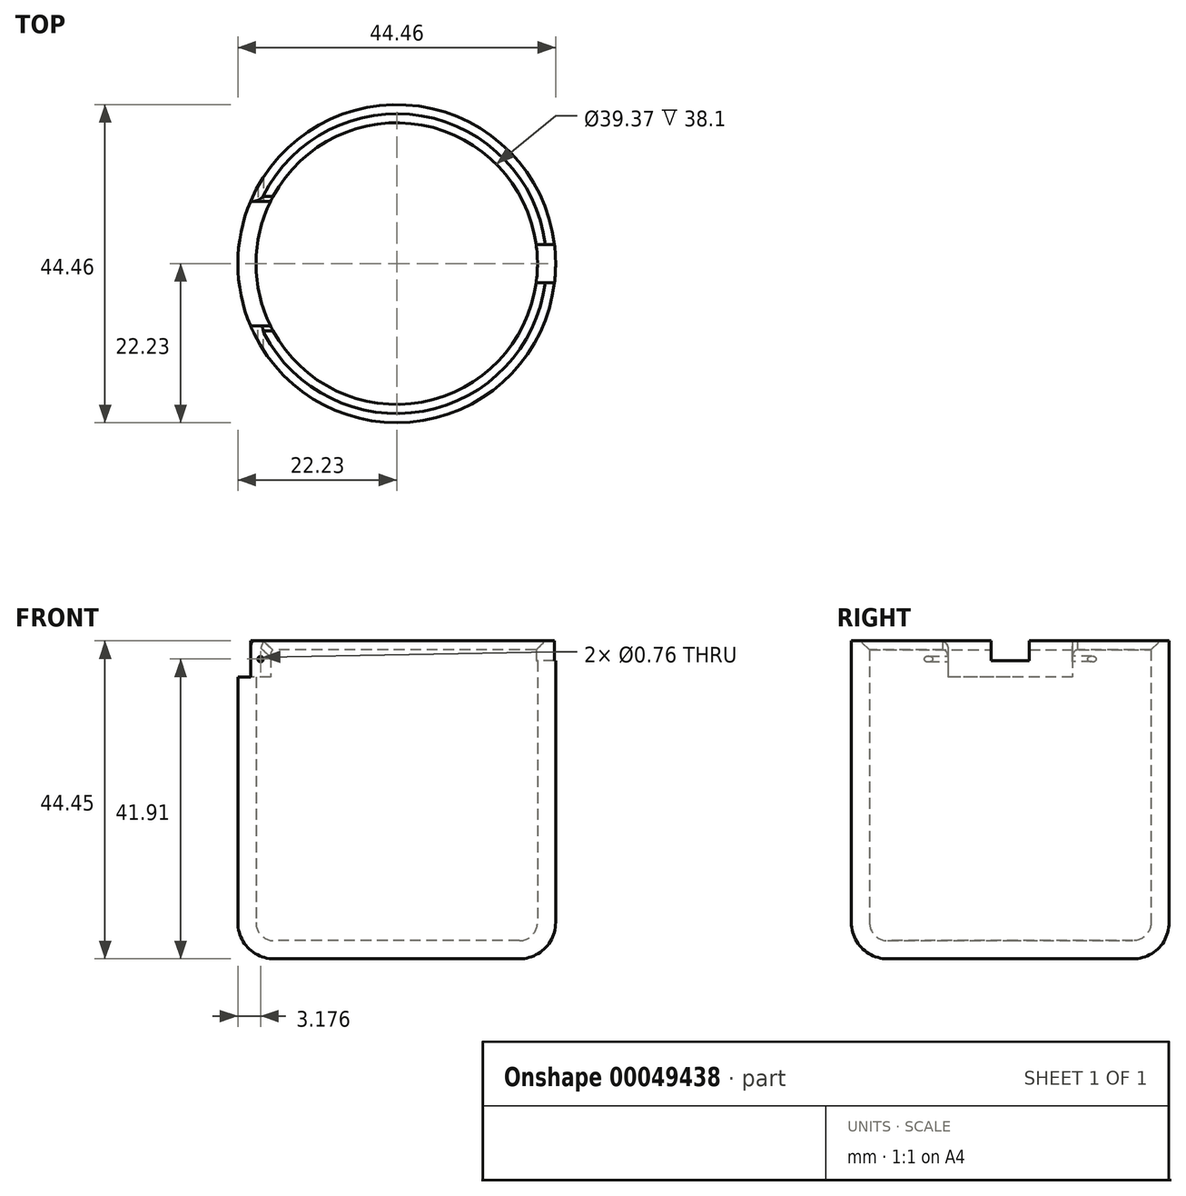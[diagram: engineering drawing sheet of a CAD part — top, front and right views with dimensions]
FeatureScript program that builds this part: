
annotation { "Feature Type Name" : "Feature", "Feature Type Description" : "" }
export const myFeature = defineFeature(function(context is Context, id is Id, definition is map)
    precondition{}
    {
        {
            var Q0;
            Q0=qCreatedBy(makeId("Top.planeOp"),FACE);
            var sketch = newSketch(context, id + "F0", { "sketchPlane" : qUnion([Q0])});
            skCircle(sketch, "E0", {"center": v(0, 0) * mm, "radius": 22.23 * mm});
            skSolve(sketch);
        }
        {
            var Q0;
            Q0=makeQuery(id+"F0.imprint","IMPRINT",FACE,{"disambiguationData":[TD([[makeQuery(id+"F0.imprint","IMPRINT",EDGE,{"derivedFrom":sQuery(id+"F0.wireOp",EDGE,"E0")}),1.0]])]});
            extrude(context, id + "F1", {"entities" : qUnion([Q0]), "depth" : 44.45 * mm});
        }
        {
            var Q0;
            Q0=makeQuery(id+"F1.opExtrude","CAP_FACE",FACE,{"disambiguationData":[OSD([sQuery(id+"F0.wireOp",EDGE,"E0")])],"isStart":true});
            fillet(context, id + "F2", {"entities" : qUnion([Q0]), "radius" : 5.08 * mm, "tangentPropagation" : true, "allowEdgeOverflow" : false});
        }
        {
            var Q0;
            Q0=makeQuery(id+"F1.opExtrude","CAP_FACE",FACE,{"disambiguationData":[OSD([sQuery(id+"F0.wireOp",EDGE,"E0")])],"isStart":false});
            shell(context, id + "F3", {"entities" : qUnion([Q0]), "thickness" : 2.54 * mm});
        }
        {
            var Q0;
            Q0=makeQuery(id+"F1.opExtrude","CAP_FACE",FACE,{"disambiguationData":[OSD([sQuery(id+"F0.wireOp",EDGE,"E0")])],"isStart":false});
            var sketch = newSketch(context, id + "F4", { "sketchPlane" : qUnion([Q0])});
            skLineSegment(sketch, "E1.rect.bottom", {"start": v(24.92, -2.67) * mm, "end": v(14.45, -2.67) * mm});
            skLineSegment(sketch, "E1.rect.top", {"start": v(24.92, 2.67) * mm, "end": v(14.45, 2.67) * mm});
            skLineSegment(sketch, "E1.rect.left", {"start": v(24.92, -2.67) * mm, "end": v(24.92, 2.67) * mm});
            skLineSegment(sketch, "E1.rect.right", {"start": v(14.45, -2.67) * mm, "end": v(14.45, 2.67) * mm});
            skPoint(sketch, "E1.rect.middle", {"position": v(19.69, 0) * mm});
            skSolve(sketch);
        }
        {
            var Q0;
            Q0=qSketchRegion(id+"F4",true);
            extrude(context, id + "F5", {"entities" : qUnion([Q0]), "operationType" : NewBodyOperationType.REMOVE, "oppositeDirection" : true, "depth" : 2.8 * mm});
        }
        {
            var Q0;
            {var subQ0=sQuery(id+"F0.wireOp",EDGE,"E0");Q0=makeQuery(id+"F3.opShell","OFFSET_EDGE",EDGE,{"disambiguationData":[OSD([subQ0]),TDD([makeQuery(id+"F1.opExtrude","CAP_EDGE",EDGE,{"disambiguationData":[OSD([subQ0])],"isStart":false})])]});}
            chamfer(context, id + "F6", {"entities" : qUnion([Q0]), "width" : 1.27 * mm, "tangentPropagation" : true});
        }
        {
            var Q0;
            Q0=makeQuery(id+"F1.opExtrude","CAP_FACE",FACE,{"disambiguationData":[OSD([sQuery(id+"F0.wireOp",EDGE,"E0")])],"isStart":false});
            var sketch = newSketch(context, id + "F7", { "sketchPlane" : qUnion([Q0])});
            skLineSegment(sketch, "E2.rect.bottom", {"start": v(-16.15, -8.72) * mm, "end": v(-28.3, -8.72) * mm});
            skLineSegment(sketch, "E2.rect.top", {"start": v(-16.15, 8.72) * mm, "end": v(-28.3, 8.72) * mm});
            skLineSegment(sketch, "E2.rect.left", {"start": v(-16.15, -8.72) * mm, "end": v(-16.15, 8.72) * mm});
            skLineSegment(sketch, "E2.rect.right", {"start": v(-28.3, -8.72) * mm, "end": v(-28.3, 8.72) * mm});
            skPoint(sketch, "E2.rect.middle", {"position": v(-22.23, 0) * mm});
            skSolve(sketch);
        }
        {
            var Q0;
            Q0=qSketchRegion(id+"F7",true);
            extrude(context, id + "F8", {"entities" : qUnion([Q0]), "operationType" : NewBodyOperationType.REMOVE, "oppositeDirection" : true, "depth" : 5.08 * mm});
        }
        {
            var Q0;
            Q0=makeQuery(id+"F8.boolean.opBoolean","COPY",FACE,{"derivedFrom":makeQuery(id+"F8.opExtrude","SWEPT_FACE",FACE,{"disambiguationData":[OSD([sQuery(id+"F7.wireOp",EDGE,"E2.rect.bottom")])]})});
            var sketch = newSketch(context, id + "F9", { "sketchPlane" : qUnion([Q0])});
            skLineSegment(sketch, "E3", {"start": v(19.05, 44.45) * mm, "end": v(19.05, 41.91) * mm, "construction": true});
            skCircle(sketch, "E4", {"center": v(19.05, 41.91) * mm, "radius": 0.38 * mm});
            skSolve(sketch);
        }
        {
            var Q0;
            Q0=makeQuery(id+"F9.imprint","IMPRINT",FACE,{"disambiguationData":[TD([[makeQuery(id+"F9.imprint","IMPRINT",EDGE,{"derivedFrom":sQuery(id+"F9.wireOp",EDGE,"E4")}),1.0]])]});
            extrude(context, id + "F10", {"entities" : qUnion([Q0]), "operationType" : NewBodyOperationType.REMOVE, "oppositeDirection" : true, "depth" : 6.35 * mm});
        }
        {
            var Q0;
            Q0=makeQuery(id+"F8.boolean.opBoolean","COPY",FACE,{"derivedFrom":makeQuery(id+"F8.opExtrude","SWEPT_FACE",FACE,{"disambiguationData":[OSD([sQuery(id+"F7.wireOp",EDGE,"E2.rect.top")])]})});
            var sketch = newSketch(context, id + "F11", { "sketchPlane" : qUnion([Q0])});
            skLineSegment(sketch, "E5", {"start": v(-19.05, 44.45) * mm, "end": v(-19.05, 41.91) * mm, "construction": true});
            skCircle(sketch, "E6", {"center": v(-19.05, 41.91) * mm, "radius": 0.38 * mm});
            skSolve(sketch);
        }
        {
            var Q0;
            Q0=qSketchRegion(id+"F11",true);
            extrude(context, id + "F12", {"entities" : qUnion([Q0]), "operationType" : NewBodyOperationType.REMOVE, "oppositeDirection" : true, "depth" : 6.35 * mm});
        }
        {
            var Q0;
            Q0=makeQuery(id+"F8.boolean.opBoolean","COPY",EDGE,{"derivedFrom":makeQuery(id+"F8.opExtrude","CAP_EDGE",EDGE,{"disambiguationData":[OSD([sQuery(id+"F7.wireOp",EDGE,"E2.rect.top")])],"isStart":true})});
            var Q1;
            Q1=makeQuery(id+"F8.boolean.opBoolean","COPY",EDGE,{"derivedFrom":makeQuery(id+"F8.opExtrude","CAP_EDGE",EDGE,{"disambiguationData":[OSD([sQuery(id+"F7.wireOp",EDGE,"E2.rect.bottom")])],"isStart":true})});
            var Q2;
            Q2=makeQuery(id+"F8.boolean.opBoolean","INTERSECT",EDGE,{"derivedFrom":[makeQuery(id+"F6.opChamfer","BLEND_FACE",FACE,{"disambiguationData":[OSD([sQuery(id+"F0.wireOp",EDGE,"E0")])]}),makeQuery(id+"F8.opExtrude","SWEPT_FACE",FACE,{"disambiguationData":[OSD([sQuery(id+"F7.wireOp",EDGE,"E2.rect.bottom")])]})]});
            var Q3;
            Q3=makeQuery(id+"F8.boolean.opBoolean","INTERSECT",EDGE,{"derivedFrom":[makeQuery(id+"F6.opChamfer","BLEND_FACE",FACE,{"disambiguationData":[OSD([sQuery(id+"F0.wireOp",EDGE,"E0")])]}),makeQuery(id+"F8.opExtrude","SWEPT_FACE",FACE,{"disambiguationData":[OSD([sQuery(id+"F7.wireOp",EDGE,"E2.rect.top")])]})]});
            fillet(context, id + "F13", {"entities" : qUnion([Q0, Q1, Q2, Q3]), "radius" : 1.02 * mm, "tangentPropagation" : true, "allowEdgeOverflow" : false});
        }
    });
